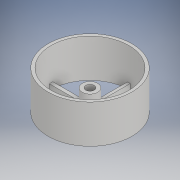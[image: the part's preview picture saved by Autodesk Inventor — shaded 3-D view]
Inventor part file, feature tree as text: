
AUTODESK INVENTOR PART (.ipt)
format: ipt  version: 2019 (Build 230136000, 136)  size: 223,744 bytes
history: native  units: in
note: dims shown in document units (in); Inventor stores cm internally (conversion verified against a paired STEP export)
features: sketch x12, extrude x11, projected_geometry x5
ambient origin geometry x8: Origin, YZ Plane, XZ Plane, XY Plane, X Axis, Y Axis, Z Axis, Center Point
bodies: Solid1 (feature_tree)
feature tree (28):
  extrude  "Extrusion1"  Depth=0.15in
  extrude  "Extrusion2"  Depth=0.1in TaperAngle=0.0deg
  extrude  "Extrusion3"  Depth=1.5in
  sketch  "Sketch6"  dims[d8=0.15in d9=0.25in d10=0.0in]
  extrude  "Extrusion7"  Depth=0.25in TaperAngle=0.0deg
  extrude  "Extrusion10"  Depth=0.875in TaperAngle=0.0deg
  extrude  "Extrusion11"  TaperAngle=0.0deg  [1 undecoded]
  extrude  "Extrusion12"  Depth=0.1in TaperAngle=0.0deg
  extrude  "Extrusion14"  Depth=3.5in
  extrude  "Extrusion15"  Depth=0.1in
  extrude  "Extrusion16"  Depth=0.25in TaperAngle=0.0deg
  extrude  "Extrusion18"  Depth=0.25in TaperAngle=0.0deg
  sketch  "Sketch1"  dims[d0=0.35in d1=0.15in]
  sketch  "Sketch2"  dims[d2=0.78in d3=0.0in d4=0.1in d5=0.0in]
  sketch  "Sketch3"  dims[d6=1.5in d7=0.75in]
  sketch  "Sketch10"  dims[d20=0.5315in d28=0.875in d29=0.0in]
  sketch  "Sketch14"  dims[d42=0.0in d43=0.0in]
  projected_geometry  "Projected Loop9"
  projected_geometry  "Projected Loop10"
  projected_geometry  "Projected Loop11"
  projected_geometry  "Projected Loop12"
  sketch  "Sketch15"  dims[d44=0.0in d45=0.1in d46=0.0in]
  sketch  "Sketch16"  dims[d47=3.25in d48=3.5in]
  sketch  "Sketch19"  dims[d49=0.1in d50=0.0in d51=3.25in]
  sketch  "Sketch20"  dims[d52=1.5in d53=0.0in d82=0.25in d83=0.0in]
  projected_geometry  "Projected Loop13"
  sketch  "Sketch21"  dims[d84=0.25in d85=0.0in d86=0.25in d87=0.0in]
  sketch  "Sketch24"  dims[d90=2.4375in d91=0.0in]
note: 1 required parameter value undecoded (feature->parameter linkage not recoverable at this tier; creation-order binding heuristic only, values carry confidence <= 0.55)
